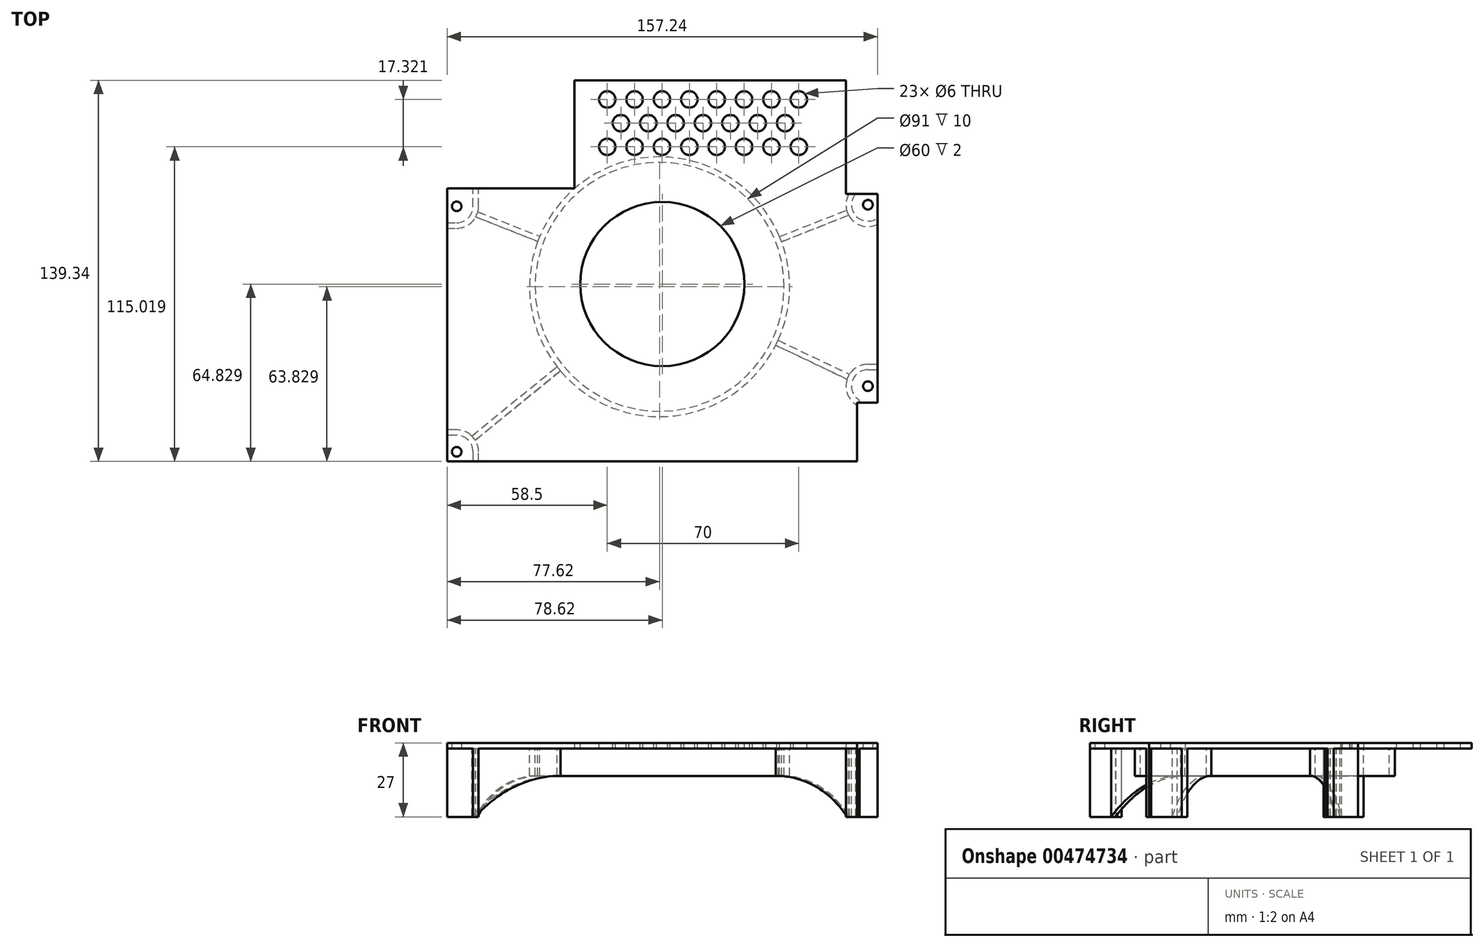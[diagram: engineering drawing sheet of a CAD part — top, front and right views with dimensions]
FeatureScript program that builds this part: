
annotation { "Feature Type Name" : "Feature", "Feature Type Description" : "" }
export const myFeature = defineFeature(function(context is Context, id is Id, definition is map)
    precondition{}
    {
        {
            var Q0;
            Q0=qCreatedBy(makeId("Top.planeOp"),FACE);
            var sketch = newSketch(context, id + "F0", { "sketchPlane" : qUnion([Q0])});
            skLineSegment(sketch, "E0.bottom", {"start": v(0, 0) * mm, "end": v(158.24, 0) * mm, "construction": true});
            skLineSegment(sketch, "E0.top", {"start": v(0, 140.34) * mm, "end": v(158.24, 140.34) * mm, "construction": true});
            skLineSegment(sketch, "E0.left", {"start": v(0, 0) * mm, "end": v(0, 140.34) * mm, "construction": true});
            skLineSegment(sketch, "E0.right", {"start": v(158.24, 0) * mm, "end": v(158.24, 140.34) * mm, "construction": true});
            skLineSegment(sketch, "E1.bottom", {"start": v(47, 139.84) * mm, "end": v(146.24, 139.84) * mm});
            skLineSegment(sketch, "E1.top", {"start": v(0.5, 0.5) * mm, "end": v(150.24, 0.5) * mm});
            skLineSegment(sketch, "E1.left", {"start": v(0.5, 100.34) * mm, "end": v(0.5, 0.5) * mm});
            skLineSegment(sketch, "E1.right", {"start": v(157.74, 98.34) * mm, "end": v(157.74, 22) * mm});
            skCircle(sketch, "E2", {"center": v(4, 93.74) * mm, "radius": 1.75 * mm});
            skCircle(sketch, "E3", {"center": v(4, 4) * mm, "radius": 1.75 * mm});
            skCircle(sketch, "E4", {"center": v(154.24, 94.34) * mm, "radius": 1.75 * mm});
            skCircle(sketch, "E5", {"center": v(154.24, 28) * mm, "radius": 1.75 * mm});
            skLineSegment(sketch, "E6", {"start": v(157.74, 22) * mm, "end": v(150.24, 22) * mm});
            skLineSegment(sketch, "E7", {"start": v(150.24, 22) * mm, "end": v(150.24, 0.5) * mm});
            skLineSegment(sketch, "E8", {"start": v(146.24, 139.84) * mm, "end": v(146.24, 98.34) * mm});
            skLineSegment(sketch, "E9", {"start": v(146.24, 98.34) * mm, "end": v(157.74, 98.34) * mm});
            skLineSegment(sketch, "E10", {"start": v(0.5, 100.34) * mm, "end": v(47, 100.34) * mm});
            skLineSegment(sketch, "E11", {"start": v(47, 100.34) * mm, "end": v(47, 139.84) * mm});
            skCircle(sketch, "E12", {"center": v(79.12, 65.33) * mm, "radius": 44.5 * mm, "construction": true});
            skSolve(sketch);
        }
        {
            var Q0;
            Q0 = qSketchRegion(id + "F0", true);
            extrude(context, id + "F1", {"entities" : qUnion([Q0]), "depth" : 2 * mm, "offsetDistance" : 25 * mm});
        }
        {
            var Q0;
            Q0=makeQuery(id+"F1.opExtrude","CAP_FACE",FACE,{"disambiguationData":[OSD([sQuery(id+"F0.wireOp",EDGE,"E1.bottom"),sQuery(id+"F0.wireOp",EDGE,"E1.top"),sQuery(id+"F0.wireOp",EDGE,"E1.left"),sQuery(id+"F0.wireOp",EDGE,"E1.right"),sQuery(id+"F0.wireOp",EDGE,"E2"),sQuery(id+"F0.wireOp",EDGE,"E3"),sQuery(id+"F0.wireOp",EDGE,"E4"),sQuery(id+"F0.wireOp",EDGE,"E5"),sQuery(id+"F0.wireOp",EDGE,"E6"),sQuery(id+"F0.wireOp",EDGE,"E7"),sQuery(id+"F0.wireOp",EDGE,"E8"),sQuery(id+"F0.wireOp",EDGE,"E9"),sQuery(id+"F0.wireOp",EDGE,"E10"),sQuery(id+"F0.wireOp",EDGE,"E11")])],"isStart":true});
            var sketch = newSketch(context, id + "F2", { "sketchPlane" : qUnion([Q0])});
            skCircle(sketch, "E13", {"center": v(78.12, -64.33) * mm, "radius": 44.5 * mm, "construction": true});
            skCircle(sketch, "E14", {"center": v(78.12, -64.33) * mm, "radius": 45.5 * mm});
            skLineSegment(sketch, "E15", {"start": v(120.56, -139.84) * mm, "end": v(122.87, -139.84) * mm});
            skLineSegment(sketch, "E16", {"start": v(4, -93.74) * mm, "end": v(78.12, -64.33) * mm, "construction": true});
            skLineSegment(sketch, "E17", {"start": v(4, -4) * mm, "end": v(78.12, -64.33) * mm, "construction": true});
            skLineSegment(sketch, "E18", {"start": v(154.24, -28) * mm, "end": v(78.12, -64.33) * mm, "construction": true});
            skLineSegment(sketch, "E19", {"start": v(78.12, -64.33) * mm, "end": v(154.24, -94.34) * mm, "construction": true});
            skArc(sketch, "E20", {"start": v(4, -10) * mm, "mid": v(8.24, -8.24) * mm, "end": v(10, -4) * mm});
            skArc(sketch, "E21", {"start": v(40.66, -35.13) * mm, "mid": v(31.17, -57.1) * mm, "end": v(33.6, -80.91) * mm});
            skArc(sketch, "E22", {"start": v(4, -12) * mm, "mid": v(6.98, -11.43) * mm, "end": v(9.52, -9.79) * mm});
            skLineSegment(sketch, "E23", {"start": v(10.79, -8.23) * mm, "end": v(41.92, -33.58) * mm});
            skLineSegment(sketch, "E24", {"start": v(9.52, -9.79) * mm, "end": v(40.66, -35.13) * mm});
            skArc(sketch, "E25.trimOffspring", {"start": v(10.79, -8.23) * mm, "mid": v(11.7, -6.2) * mm, "end": v(12, -4) * mm});
            skArc(sketch, "E26", {"start": v(10, -93.74) * mm, "mid": v(8.24, -89.5) * mm, "end": v(4, -87.74) * mm});
            skLineSegment(sketch, "E27", {"start": v(4, -10) * mm, "end": v(0.5, -10) * mm});
            skLineSegment(sketch, "E28", {"start": v(4, -12) * mm, "end": v(0.5, -12) * mm});
            skLineSegment(sketch, "E29", {"start": v(0.5, -10) * mm, "end": v(0.5, -12) * mm});
            skLineSegment(sketch, "E30", {"start": v(10, -4) * mm, "end": v(10, -0.5) * mm});
            skLineSegment(sketch, "E31", {"start": v(12, -0.5) * mm, "end": v(12, -4) * mm});
            skLineSegment(sketch, "E32", {"start": v(10, -0.5) * mm, "end": v(12, -0.5) * mm});
            skLineSegment(sketch, "E33", {"start": v(0.5, -85.74) * mm, "end": v(4, -85.74) * mm});
            skLineSegment(sketch, "E34", {"start": v(0.5, -87.74) * mm, "end": v(4, -87.74) * mm});
            skLineSegment(sketch, "E35", {"start": v(12, -93.74) * mm, "end": v(12, -100.34) * mm});
            skLineSegment(sketch, "E36", {"start": v(10, -93.74) * mm, "end": v(10, -100.34) * mm});
            skArc(sketch, "E37.trimOffspring", {"start": v(12, -93.74) * mm, "mid": v(11.94, -92.73) * mm, "end": v(11.75, -91.74) * mm});
            skLineSegment(sketch, "E38", {"start": v(0.5, -85.74) * mm, "end": v(0.5, -87.74) * mm});
            skLineSegment(sketch, "E39", {"start": v(10, -100.34) * mm, "end": v(12, -100.34) * mm});
            skLineSegment(sketch, "E40", {"start": v(11, -89.88) * mm, "end": v(33.6, -80.91) * mm});
            skLineSegment(sketch, "E41", {"start": v(11.75, -91.74) * mm, "end": v(34.35, -82.77) * mm});
            skArc(sketch, "E42.trimOffspring", {"start": v(11, -89.88) * mm, "mid": v(8.07, -86.85) * mm, "end": v(4, -85.74) * mm});
            skArc(sketch, "E43.trimOffspring", {"start": v(34.35, -82.77) * mm, "mid": v(78.17, -111.83) * mm, "end": v(121.93, -82.68) * mm});
            skArc(sketch, "E44", {"start": v(151.17, -22.85) * mm, "mid": v(148.46, -29.6) * mm, "end": v(154.24, -34) * mm});
            skArc(sketch, "E45", {"start": v(150.24, -21.07) * mm, "mid": v(146.76, -25.15) * mm, "end": v(146.65, -30.52) * mm});
            skLineSegment(sketch, "E46", {"start": v(154.24, -34) * mm, "end": v(157.74, -34) * mm});
            skLineSegment(sketch, "E47", {"start": v(154.24, -36) * mm, "end": v(157.74, -36) * mm});
            skLineSegment(sketch, "E48", {"start": v(157.74, -34) * mm, "end": v(157.74, -36) * mm});
            skLineSegment(sketch, "E49", {"start": v(150.24, -21.07) * mm, "end": v(150.24, -22) * mm});
            skLineSegment(sketch, "E50", {"start": v(150.24, -22) * mm, "end": v(151.17, -22) * mm});
            skLineSegment(sketch, "E51", {"start": v(120.55, -42.97) * mm, "end": v(146.65, -30.52) * mm});
            skLineSegment(sketch, "E52", {"start": v(121.4, -44.78) * mm, "end": v(147.5, -32.32) * mm});
            skArc(sketch, "E53.trimOffspring", {"start": v(120.55, -42.97) * mm, "mid": v(83.76, -17.16) * mm, "end": v(41.92, -33.58) * mm});
            skArc(sketch, "E54.trimOffspring", {"start": v(147.5, -32.32) * mm, "mid": v(150.4, -35.02) * mm, "end": v(154.24, -36) * mm});
            skArc(sketch, "E55", {"start": v(157.74, -89.47) * mm, "mid": v(149.78, -90.33) * mm, "end": v(149.77, -98.34) * mm});
            skArc(sketch, "E56", {"start": v(157.74, -87.15) * mm, "mid": v(151.81, -86.72) * mm, "end": v(147.22, -90.5) * mm});
            skLineSegment(sketch, "E57", {"start": v(147.31, -98.34) * mm, "end": v(149.77, -98.34) * mm});
            skLineSegment(sketch, "E58", {"start": v(157.74, -89.47) * mm, "end": v(157.74, -87.15) * mm});
            skLineSegment(sketch, "E59", {"start": v(122.67, -80.82) * mm, "end": v(147.22, -90.5) * mm});
            skLineSegment(sketch, "E60", {"start": v(121.93, -82.68) * mm, "end": v(146.49, -92.36) * mm});
            skArc(sketch, "E61.trimOffspring", {"start": v(122.67, -80.82) * mm, "mid": v(125.6, -62.67) * mm, "end": v(121.4, -44.78) * mm});
            skArc(sketch, "E62.trimOffspring", {"start": v(146.49, -92.36) * mm, "mid": v(146.31, -95.43) * mm, "end": v(147.31, -98.34) * mm});
            skLineSegment(sketch, "E63", {"start": v(151.17, -22) * mm, "end": v(151.17, -22.85) * mm});
            skSolve(sketch);
        }
        {
            var Q0;
            Q0 = qSketchRegion(id + "F2", true);
            extrude(context, id + "F3", {"entities" : qUnion([Q0]), "operationType" : NewBodyOperationType.ADD, "depth" : 25 * mm, "offsetDistance" : 25 * mm});
        }
        {
            var Q0;
            Q0=makeQuery(id+"F3.opExtrude","CAP_FACE",FACE,{"disambiguationData":[OSD([sQuery(id+"F2.wireOp",EDGE,"E14"),sQuery(id+"F2.wireOp",EDGE,"E20"),sQuery(id+"F2.wireOp",EDGE,"E21"),sQuery(id+"F2.wireOp",EDGE,"E22"),sQuery(id+"F2.wireOp",EDGE,"E23"),sQuery(id+"F2.wireOp",EDGE,"E24"),sQuery(id+"F2.wireOp",EDGE,"E25.trimOffspring"),sQuery(id+"F2.wireOp",EDGE,"E26"),sQuery(id+"F2.wireOp",EDGE,"E27"),sQuery(id+"F2.wireOp",EDGE,"E28"),sQuery(id+"F2.wireOp",EDGE,"E29"),sQuery(id+"F2.wireOp",EDGE,"E30"),sQuery(id+"F2.wireOp",EDGE,"E31"),sQuery(id+"F2.wireOp",EDGE,"E32"),sQuery(id+"F2.wireOp",EDGE,"E33"),sQuery(id+"F2.wireOp",EDGE,"E34"),sQuery(id+"F2.wireOp",EDGE,"E35"),sQuery(id+"F2.wireOp",EDGE,"E36"),sQuery(id+"F2.wireOp",EDGE,"E37.trimOffspring"),sQuery(id+"F2.wireOp",EDGE,"E38"),sQuery(id+"F2.wireOp",EDGE,"E39"),sQuery(id+"F2.wireOp",EDGE,"E40"),sQuery(id+"F2.wireOp",EDGE,"E41"),sQuery(id+"F2.wireOp",EDGE,"E42.trimOffspring"),sQuery(id+"F2.wireOp",EDGE,"E43.trimOffspring"),sQuery(id+"F2.wireOp",EDGE,"E44"),sQuery(id+"F2.wireOp",EDGE,"E45"),sQuery(id+"F2.wireOp",EDGE,"E46"),sQuery(id+"F2.wireOp",EDGE,"E47"),sQuery(id+"F2.wireOp",EDGE,"E48"),sQuery(id+"F2.wireOp",EDGE,"E49"),sQuery(id+"F2.wireOp",EDGE,"E50"),sQuery(id+"F2.wireOp",EDGE,"E51"),sQuery(id+"F2.wireOp",EDGE,"E52"),sQuery(id+"F2.wireOp",EDGE,"E53.trimOffspring"),sQuery(id+"F2.wireOp",EDGE,"E54.trimOffspring"),sQuery(id+"F2.wireOp",EDGE,"E55"),sQuery(id+"F2.wireOp",EDGE,"E56"),sQuery(id+"F2.wireOp",EDGE,"E57"),sQuery(id+"F2.wireOp",EDGE,"E58"),sQuery(id+"F2.wireOp",EDGE,"E59"),sQuery(id+"F2.wireOp",EDGE,"E60"),sQuery(id+"F2.wireOp",EDGE,"E61.trimOffspring"),sQuery(id+"F2.wireOp",EDGE,"E62.trimOffspring"),sQuery(id+"F2.wireOp",EDGE,"E63")])],"isStart":false});
            var sketch = newSketch(context, id + "F4", { "sketchPlane" : qUnion([Q0])});
            skCircle(sketch, "E64", {"center": v(78.12, -64.33) * mm, "radius": 45.5 * mm});
            skCircle(sketch, "E65", {"center": v(78.12, -64.33) * mm, "radius": 47.5 * mm});
            skSolve(sketch);
        }
        {
            var Q0;
            Q0 = qSketchRegion(id + "F4", true);
            extrude(context, id + "F5", {"entities" : qUnion([Q0]), "operationType" : NewBodyOperationType.REMOVE, "oppositeDirection" : true, "depth" : 15 * mm, "offsetDistance" : 25 * mm});
        }
        {
            var Q0;
            Q0=makeQuery(id+"F3.opExtrude","SWEPT_FACE",FACE,{"disambiguationData":[OSD([sQuery(id+"F2.wireOp",EDGE,"E24")])]});
            var sketch = newSketch(context, id + "F6", { "sketchPlane" : qUnion([Q0])});
            skArc(sketch, "E66", {"start": v(-13.56, -25) * mm, "mid": v(-32.28, -13.87) * mm, "end": v(-53.7, -10) * mm});
            skLineSegment(sketch, "E67", {"start": v(-53.7, -10) * mm, "end": v(-13.56, -10) * mm, "construction": true});
            skLineSegment(sketch, "E68", {"start": v(-53.7, -10) * mm, "end": v(-53.7, -25) * mm});
            skLineSegment(sketch, "E69", {"start": v(-53.7, -25) * mm, "end": v(-13.56, -25) * mm});
            skSolve(sketch);
        }
        {
            var Q0;
            Q0 = qSketchRegion(id + "F6", true);
            extrude(context, id + "F7", {"entities" : qUnion([Q0]), "operationType" : NewBodyOperationType.REMOVE, "endBound" : BoundingType.UP_TO_NEXT, "oppositeDirection" : true, "depth" : 25 * mm, "offsetDistance" : 25 * mm});
        }
        {
            var Q0;
            Q0=makeQuery(id+"F3.opExtrude","SWEPT_FACE",FACE,{"disambiguationData":[OSD([sQuery(id+"F2.wireOp",EDGE,"E41")])]});
            var sketch = newSketch(context, id + "F8", { "sketchPlane" : qUnion([Q0])});
            skArc(sketch, "E70", {"start": v(22.92, -25) * mm, "mid": v(12.89, -14.05) * mm, "end": v(-1.4, -10) * mm});
            skLineSegment(sketch, "E71", {"start": v(-1.4, -10) * mm, "end": v(22.92, -10) * mm, "construction": true});
            skLineSegment(sketch, "E72", {"start": v(22.92, -25) * mm, "end": v(-1.4, -25) * mm});
            skLineSegment(sketch, "E73", {"start": v(-1.4, -25) * mm, "end": v(-1.4, -10) * mm});
            skSolve(sketch);
        }
        {
            var Q0;
            Q0 = qSketchRegion(id + "F8", true);
            extrude(context, id + "F9", {"entities" : qUnion([Q0]), "operationType" : NewBodyOperationType.REMOVE, "endBound" : BoundingType.UP_TO_NEXT, "oppositeDirection" : true, "depth" : 25 * mm, "offsetDistance" : 25 * mm});
        }
        {
            var Q0;
            Q0=makeQuery(id+"F3.opExtrude","SWEPT_FACE",FACE,{"disambiguationData":[OSD([sQuery(id+"F2.wireOp",EDGE,"E60")])]});
            var sketch = newSketch(context, id + "F10", { "sketchPlane" : qUnion([Q0])});
            skLineSegment(sketch, "E74", {"start": v(-143.76, -10) * mm, "end": v(-143.76, -25) * mm});
            skLineSegment(sketch, "E75", {"start": v(-143.76, -25) * mm, "end": v(-170.16, -25) * mm});
            skLineSegment(sketch, "E76", {"start": v(-143.76, -10) * mm, "end": v(-170.16, -10) * mm, "construction": true});
            skArc(sketch, "E77", {"start": v(-143.76, -10) * mm, "mid": v(-158.94, -14.01) * mm, "end": v(-170.16, -25) * mm});
            skSolve(sketch);
        }
        {
            var Q0;
            Q0 = qSketchRegion(id + "F10", true);
            extrude(context, id + "F11", {"entities" : qUnion([Q0]), "operationType" : NewBodyOperationType.REMOVE, "endBound" : BoundingType.UP_TO_NEXT, "oppositeDirection" : true, "depth" : 25 * mm, "offsetDistance" : 25 * mm});
        }
        {
            var Q0;
            Q0=makeQuery(id+"F3.opExtrude","SWEPT_FACE",FACE,{"disambiguationData":[OSD([sQuery(id+"F2.wireOp",EDGE,"E52")])]});
            var sketch = newSketch(context, id + "F12", { "sketchPlane" : qUnion([Q0])});
            skLineSegment(sketch, "E78", {"start": v(-90.28, -10) * mm, "end": v(-90.28, -25) * mm});
            skLineSegment(sketch, "E79", {"start": v(-90.28, -25) * mm, "end": v(-119.2, -25) * mm});
            skLineSegment(sketch, "E80", {"start": v(-90.28, -10) * mm, "end": v(-119.2, -10) * mm, "construction": true});
            skArc(sketch, "E81", {"start": v(-90.28, -10) * mm, "mid": v(-106.57, -13.97) * mm, "end": v(-119.2, -25) * mm});
            skSolve(sketch);
        }
        {
            var Q0;
            Q0 = qSketchRegion(id + "F12", true);
            extrude(context, id + "F13", {"entities" : qUnion([Q0]), "operationType" : NewBodyOperationType.REMOVE, "endBound" : BoundingType.UP_TO_NEXT, "oppositeDirection" : true, "depth" : 25 * mm, "offsetDistance" : 25 * mm});
        }
        {
            var Q0;
            Q0=makeQuery(id+"F1.opExtrude","CAP_FACE",FACE,{"disambiguationData":[OSD([sQuery(id+"F0.wireOp",EDGE,"E1.bottom"),sQuery(id+"F0.wireOp",EDGE,"E1.top"),sQuery(id+"F0.wireOp",EDGE,"E1.left"),sQuery(id+"F0.wireOp",EDGE,"E1.right"),sQuery(id+"F0.wireOp",EDGE,"E2"),sQuery(id+"F0.wireOp",EDGE,"E3"),sQuery(id+"F0.wireOp",EDGE,"E4"),sQuery(id+"F0.wireOp",EDGE,"E5"),sQuery(id+"F0.wireOp",EDGE,"E6"),sQuery(id+"F0.wireOp",EDGE,"E7"),sQuery(id+"F0.wireOp",EDGE,"E8"),sQuery(id+"F0.wireOp",EDGE,"E9"),sQuery(id+"F0.wireOp",EDGE,"E10"),sQuery(id+"F0.wireOp",EDGE,"E11")])],"isStart":false});
            var sketch = newSketch(context, id + "F14", { "sketchPlane" : qUnion([Q0])});
            skCircle(sketch, "E82", {"center": v(59, 132.84) * mm, "radius": 3 * mm});
            skCircle(sketch, "E83.1.0.0", {"center": v(69, 132.84) * mm, "radius": 3 * mm});
            skCircle(sketch, "E83.2.0.0", {"center": v(79, 132.84) * mm, "radius": 3 * mm});
            skCircle(sketch, "E83.3.0.0", {"center": v(89, 132.84) * mm, "radius": 3 * mm});
            skCircle(sketch, "E83.4.0.0", {"center": v(99, 132.84) * mm, "radius": 3 * mm});
            skCircle(sketch, "E83.5.0.0", {"center": v(109, 132.84) * mm, "radius": 3 * mm});
            skCircle(sketch, "E83.6.0.0", {"center": v(119, 132.84) * mm, "radius": 3 * mm});
            skCircle(sketch, "E83.7.0.0", {"center": v(129, 132.84) * mm, "radius": 3 * mm});
            skLineSegment(sketch, "E83.direction1", {"start": v(59, 132.84) * mm, "end": v(69, 132.84) * mm, "construction": true});
            skLineSegment(sketch, "E84", {"start": v(59, 132.84) * mm, "end": v(64, 124.18) * mm, "construction": true});
            skLineSegment(sketch, "E85", {"start": v(64, 124.18) * mm, "end": v(69, 132.84) * mm, "construction": true});
            skCircle(sketch, "E86", {"center": v(64, 124.18) * mm, "radius": 3 * mm});
            skCircle(sketch, "E87.1.0.0", {"center": v(74, 124.18) * mm, "radius": 3 * mm});
            skCircle(sketch, "E87.2.0.0", {"center": v(84, 124.18) * mm, "radius": 3 * mm});
            skCircle(sketch, "E87.3.0.0", {"center": v(94, 124.18) * mm, "radius": 3 * mm});
            skCircle(sketch, "E87.4.0.0", {"center": v(104, 124.18) * mm, "radius": 3 * mm});
            skCircle(sketch, "E87.5.0.0", {"center": v(114, 124.18) * mm, "radius": 3 * mm});
            skCircle(sketch, "E87.6.0.0", {"center": v(124, 124.18) * mm, "radius": 3 * mm});
            skLineSegment(sketch, "E87.direction1", {"start": v(64, 124.18) * mm, "end": v(74, 124.18) * mm, "construction": true});
            skLineSegment(sketch, "E88", {"start": v(64, 124.18) * mm, "end": v(59, 115.52) * mm, "construction": true});
            skLineSegment(sketch, "E89", {"start": v(59, 115.52) * mm, "end": v(69, 115.52) * mm, "construction": true});
            skLineSegment(sketch, "E90", {"start": v(69, 115.52) * mm, "end": v(64, 124.18) * mm, "construction": true});
            skCircle(sketch, "E91", {"center": v(59, 115.52) * mm, "radius": 3 * mm});
            skCircle(sketch, "E92.1.0.0", {"center": v(69, 115.52) * mm, "radius": 3 * mm});
            skCircle(sketch, "E92.2.0.0", {"center": v(79, 115.52) * mm, "radius": 3 * mm});
            skCircle(sketch, "E92.3.0.0", {"center": v(89, 115.52) * mm, "radius": 3 * mm});
            skCircle(sketch, "E92.4.0.0", {"center": v(99, 115.52) * mm, "radius": 3 * mm});
            skCircle(sketch, "E92.5.0.0", {"center": v(109, 115.52) * mm, "radius": 3 * mm});
            skCircle(sketch, "E92.6.0.0", {"center": v(119, 115.52) * mm, "radius": 3 * mm});
            skCircle(sketch, "E92.7.0.0", {"center": v(129, 115.52) * mm, "radius": 3 * mm});
            skCircle(sketch, "E93", {"center": v(79.12, 65.33) * mm, "radius": 30 * mm});
            skSolve(sketch);
        }
        {
            var Q0;
            Q0 = qSketchRegion(id + "F14", true);
            extrude(context, id + "F15", {"entities" : qUnion([Q0]), "operationType" : NewBodyOperationType.REMOVE, "endBound" : BoundingType.UP_TO_NEXT, "oppositeDirection" : true, "depth" : 25 * mm, "offsetDistance" : 25 * mm});
        }
    });
